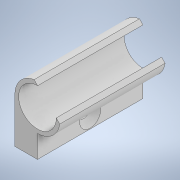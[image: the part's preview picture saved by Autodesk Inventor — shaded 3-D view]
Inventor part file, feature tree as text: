
AUTODESK INVENTOR PART (.ipt)
format: ipt  version: 2022 (Build 260153070, 153G)  size: 279,552 bytes
history: native  units: in
note: dims shown in document units (in); Inventor stores cm internally (conversion verified against a paired STEP export)
features: sketch x4, extrude x3, hole x1
ambient origin geometry x8: Origin, YZ Plane, XZ Plane, XY Plane, X Axis, Y Axis, Z Axis, Center Point
bodies: Body1 (feature_tree)
feature tree (8):
  extrude  "Extrusion3"  Depth=0.05in
  extrude  "Extrusion4"  Depth=0.35in
  hole  "Hole1"  [1 undecoded]
  extrude  "Text"  Depth=0.045in
  sketch  "Sketch4"  dims[d10=0.5in d11=0.05in]
  sketch  "Sketch5"  dims[d12=45.0deg d13=0.35in]
  sketch  "Sketch6"  dims[d14=1.4in d15=0.0in]
  sketch  "Sketch10"  dims[d16=0.3in d17=1.4in d18=0.0in d19=0.138in d20=0.75in d21=0.28in d22=0.25in d23=0.5635in d24=0.29in d25=0.0in d28=0.045in d29=0.0in d30=0.15in d31=0.0in]
note: 1 required parameter value undecoded (feature->parameter linkage not recoverable at this tier; creation-order binding heuristic only, values carry confidence <= 0.55)
